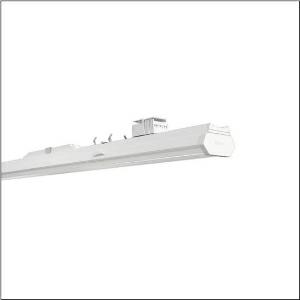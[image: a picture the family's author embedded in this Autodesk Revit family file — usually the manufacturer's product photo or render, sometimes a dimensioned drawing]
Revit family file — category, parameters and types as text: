
# Revit family: licross_r__11_dc_protected_54td1bdn69xg_faa1
name_source: partatom
category: Lighting Fixtures
units: mm (PartAtom-declared; Revit-internal decimal feet)

## family parameters
Cut with Voids When Loaded = No
Host = Face
Light Source = No
Part Type = Normal
Room Calculation Point = No
Round Connector Dimension = Use Diameter
Shared = No

## types (1)
- --- (1 x LED, 9140 lm, 57 W, 6500K)
    Apparent Load = 57 VA
    CIE Flux Codes = 54 82 95 97 100
    Color Rendering = 80
    Color Temperature = 6500K
    Default Elevation = 1800 mm
    Description = Licross® 11 DC Protected, luminaire insert, of sheet steel, galvanised, coil coated, white, length: 1.500mm, width: 90mm, height: 101mm, LED rated luminous flux: 9.140lm, light colour: 865, control gear: DALI 2, with plug, 5-pole, without phase selection, mains connection: 650V, DC, rated input power: 57W, internal wiring halogen-free, option to choose between normal mains or equivalent power supply by moving two contact pins without tools before inserting it into the trunking rail, primary optical cover: cover, of PMMA, light emission: direct distribution, primary light characteristic: symmetric, protection rating (complete): IP54, insulation class (complete): insulation class I (protective earthing), certification: CE, UKCA, protection symbol: D if used in an environment with non-conductive dust loads with corresponding accessories, impact resistance: IK06, permissible ambient temperature for indoor applications: -30..+35°C, corresponds to IFS (International Featured Standards) requirements for safety and quality in the food industry, reducing of maximum allowable ambient temperature of 5°C with ceiling mounting, LABS conformity tested according to VDMA 24364:2018-05, packaging unit: 1 piece
    Height = 92 mm
    Lamp = 1 x LED
    Lamp Light Flux = 9140 lm
    Lamp Power = 57 W
    Lamp count = 1
    Length = 1500 mm
    Luminous efficacy = 160 lm/W
    Manufacturer = Siteco
    ModVariant = No
    Model = 54TD1BDN69XG
    Mounting Place = Ceiling
    Mounting Type = Pendant
    Number of Poles = 1
    OnlyDefault = Yes
    Power Factor = 1
    Product Name = Licross® 11 DC Protected
    Product group = luminaire insert | ceiling pendant
    ProductGroupID = 902
    Protection Class = Protection class I
    Protection Degree = IP 54
    RLX_Detail_Level = 1
    RLX_Emergency_Light_Flux = 0 lm
    RLX_Emergency_Type = 0
    RLX_Emergency_Type_DB = No
    RlxData = <blob elided: 24477 chars, md5=af6480e1>
    Socket = socket
    Standby Power = 0 W
    System Light Flux = 9140 lm
    System Power = 57 W
    Type Comments = factory setting: luminous flux: 100 % | dim-lin: 254 | 379 mA
    Type Image = l_1256145.jpg
    URL = http://relux.com
    VarID = @adj_018655
    Voltage = 0 V
    Weight = 0.00 kg
    Width = 88 mm

## geometry (parser evidence)
native form markers: Blend x4, Sweep x11
no freeform markers — native parametric forms only
